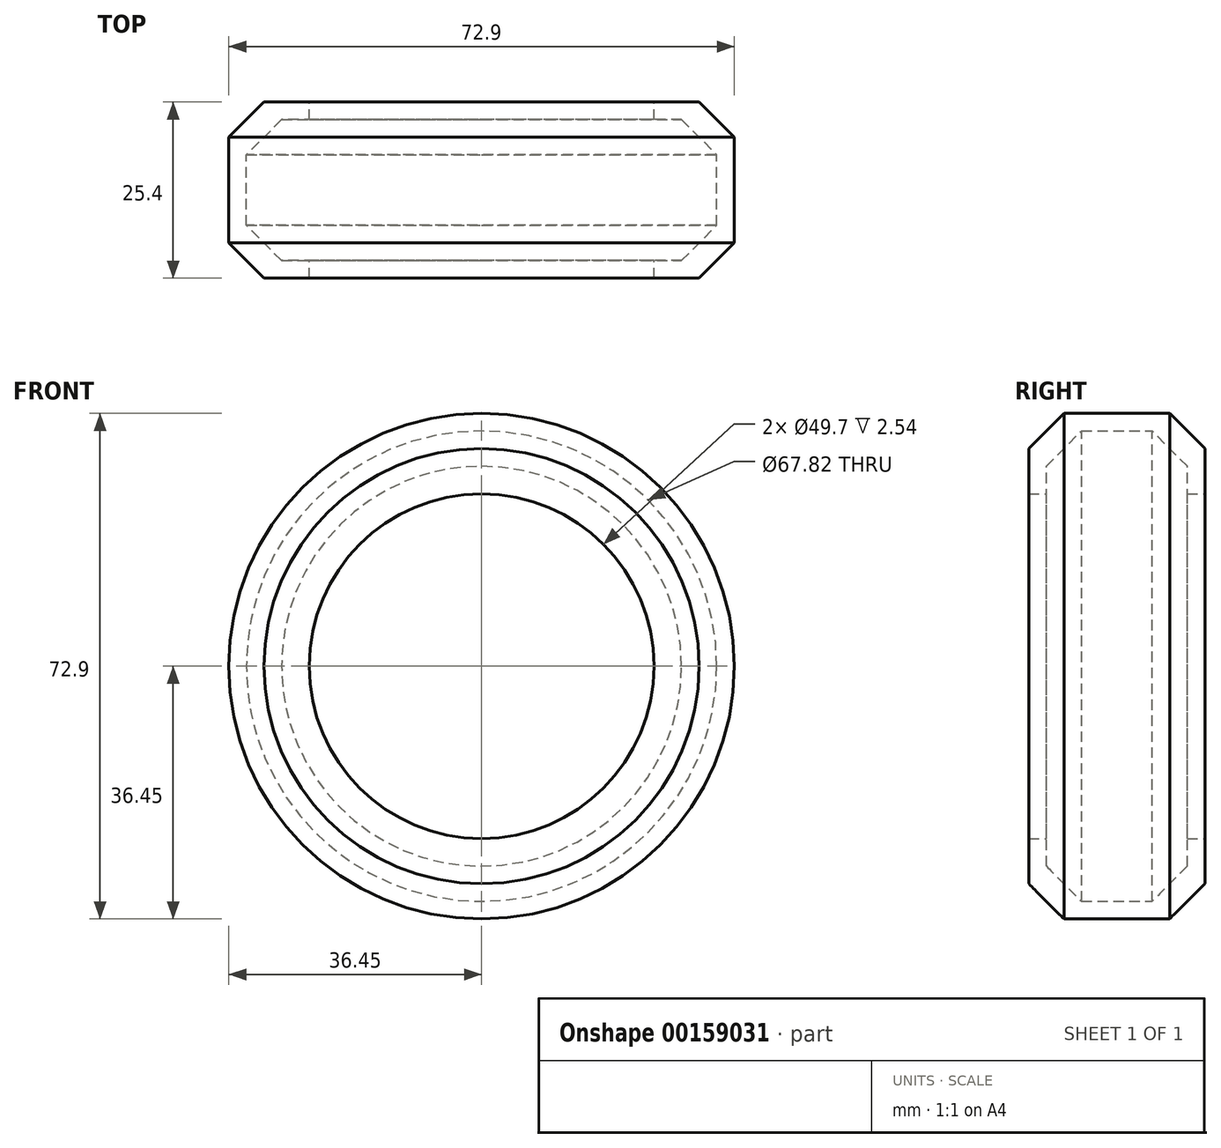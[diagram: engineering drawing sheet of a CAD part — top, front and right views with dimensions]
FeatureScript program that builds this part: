
annotation { "Feature Type Name" : "Feature", "Feature Type Description" : "" }
export const myFeature = defineFeature(function(context is Context, id is Id, definition is map)
    precondition{}
    {
        {
            var Q0;
            Q0=qCreatedBy(makeId("Front.planeOp"),FACE);
            var sketch = newSketch(context, id + "F0", { "sketchPlane" : qUnion([Q0])});
            skCircle(sketch, "E0", {"center": v(0, 0) * mm, "radius": 36.45 * mm});
            skCircle(sketch, "E1", {"center": v(0, 0) * mm, "radius": 24.85 * mm});
            skSolve(sketch);
        }
        {
            var Q0;
            Q0=makeQuery(id+"F0.imprint","IMPRINT",FACE,{"disambiguationData":[TD([[makeQuery(id+"F0.imprint","IMPRINT",EDGE,{"derivedFrom":sQuery(id+"F0.wireOp",EDGE,"E0")}),1.0]])]});
            extrude(context, id + "F1", {"entities" : qUnion([Q0]), "depth" : 25.4 * mm});
        }
        {
            var Q0;
            Q0=makeQuery(id+"F1.opExtrude","SWEPT_FACE",FACE,{"disambiguationData":[OSD([sQuery(id+"F0.wireOp",EDGE,"E1")])]});
            shell(context, id + "F2", {"entities" : qUnion([Q0]), "thickness" : 2.54 * mm});
        }
        {
            var Q0;
            Q0=makeQuery(id+"F2.opShell","OFFSET_FACE",FACE,{"disambiguationData":[OSD([sQuery(id+"F0.wireOp",EDGE,"E0")])]});
            chamfer(context, id + "F3", {"entities" : qUnion([Q0]), "width" : 5.08 * mm, "tangentPropagation" : true});
        }
        {
            var Q0;
            Q0=makeQuery(id+"F1.opExtrude","SWEPT_FACE",FACE,{"disambiguationData":[OSD([sQuery(id+"F0.wireOp",EDGE,"E0")])]});
            chamfer(context, id + "F4", {"entities" : qUnion([Q0]), "width" : 5.08 * mm, "tangentPropagation" : true});
        }
    });
